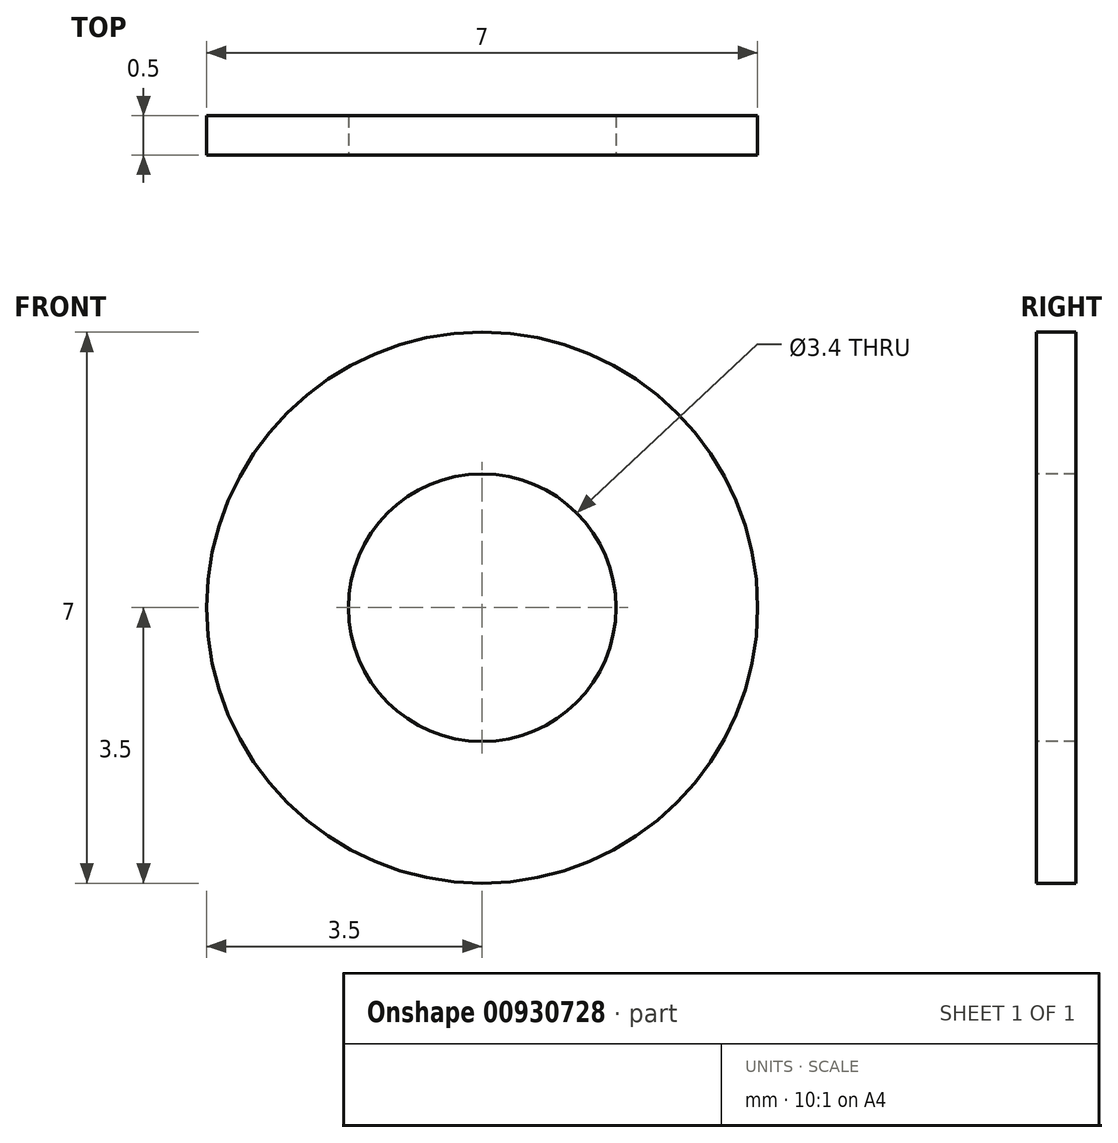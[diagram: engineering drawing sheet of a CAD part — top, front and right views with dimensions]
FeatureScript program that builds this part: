
annotation { "Feature Type Name" : "Feature", "Feature Type Description" : "" }
export const myFeature = defineFeature(function(context is Context, id is Id, definition is map)
    precondition{}
    {
        {
            var Q0;
            Q0=qCreatedBy(makeId("Front.planeOp"),FACE);
            var sketch = newSketch(context, id + "F0", { "sketchPlane" : qUnion([Q0])});
            skCircle(sketch, "E0", {"center": v(0, 0) * mm, "radius": 1.7 * mm});
            skCircle(sketch, "E1", {"center": v(0, 0) * mm, "radius": 3.5 * mm});
            skSolve(sketch);
        }
        {
            var Q0;
            Q0=makeQuery(id+"F0.imprint","IMPRINT",FACE,{"disambiguationData":[TD([[makeQuery(id+"F0.imprint","IMPRINT",EDGE,{"derivedFrom":sQuery(id+"F0.wireOp",EDGE,"E0")}),-1.0]])]});
            extrude(context, id + "F1", {"entities" : qUnion([Q0]), "oppositeDirection" : true, "depth" : 0.5 * mm, "offsetDistance" : 25 * mm});
        }
    });
